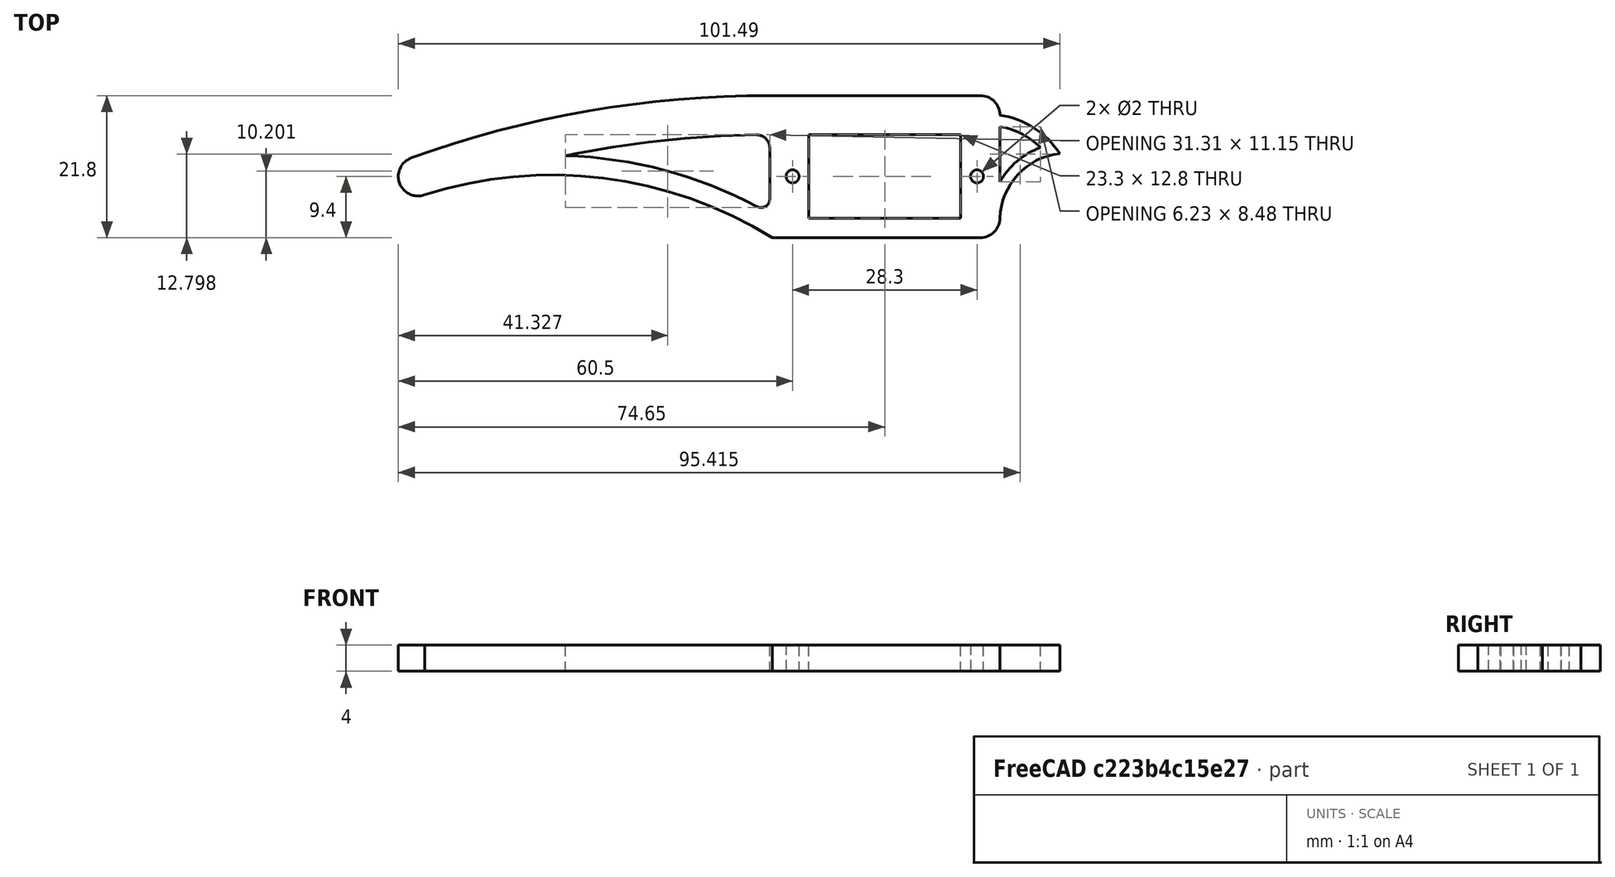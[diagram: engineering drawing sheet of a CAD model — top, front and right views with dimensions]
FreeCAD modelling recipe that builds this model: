
FCSTD DOCUMENT  (FreeCAD 0.21R33771 (Git))
Label: крак-база
License: All rights reserved
LicenseURL: https://en.wikipedia.org/wiki/All_rights_reserved
objects: Sketcher::SketchObject×1, PartDesign::Pad×1, PartDesign::Body×1
note: 4 computed .brp shape members not serialized (recipe doc carries the construction recipe); baked Part::Feature solids carry a one-line shape summary decoded from their .brp

FEATURE [Sketcher::SketchObject] Sketch
  FullyConstrained = true
  MapMode = 5
  Support = -> [XY_Plane]
  sketch-geometry (26):
    g0: LineSegment StartX=-11.65 StartY=-6.4 StartZ=0 EndX=-11.65 EndY=6.4 EndZ=0
    g1: LineSegment StartX=-11.65 StartY=6.4 StartZ=0 EndX=11.65 EndY=6.4 EndZ=0
    g2: LineSegment StartX=11.65 StartY=6.4 StartZ=0 EndX=11.65 EndY=-6.4 EndZ=0
    g3: LineSegment StartX=11.65 StartY=-6.4 StartZ=0 EndX=-11.65 EndY=-6.4 EndZ=0
    g4: GeomPoint X=0 Y=0 Z=0
    g5: LineSegment StartX=-17.65 StartY=12.4 StartZ=0 EndX=14.65 EndY=12.4 EndZ=0
    g6: LineSegment StartX=17.65 StartY=7.63618 StartZ=0 EndX=17.65 EndY=-0.84 EndZ=0
    g7: LineSegment StartX=14.65 StartY=-9.4 StartZ=0 EndX=-17.27 EndY=-9.4 EndZ=0
    g8: LineSegment StartX=-17.6662 StartY=-3.46627 StartZ=0 EndX=-17.6662 EndY=4.38856 EndZ=0
    g9: ArcOfCircle CenterX=-71.65 CenterY=0 CenterZ=0 NormalX=0 NormalY=0 NormalZ=1 AngleXU=0 Radius=3 StartAngle=1.91771 EndAngle=5.06056
    g10: ArcOfCircle CenterX=14.65 CenterY=9.4 CenterZ=0 NormalX=0 NormalY=0 NormalZ=1 AngleXU=0 Radius=3 StartAngle=6.28319 EndAngle=7.85398
    g11: GeomPoint X=17.65 Y=12.4 Z=0
    g12: ArcOfCircle CenterX=14.65 CenterY=-6.4 CenterZ=0 NormalX=0 NormalY=0 NormalZ=1 AngleXU=0 Radius=3 StartAngle=4.71239 EndAngle=6.28319
    g13: GeomPoint X=17.65 Y=-9.4 Z=0
    g14: ArcOfCircle CenterX=-18.0008 CenterY=-148.391 CenterZ=0 NormalX=0 NormalY=0 NormalZ=1 AngleXU=0 Radius=160.792 StartAngle=1.56861 EndAngle=1.91771
    g15: ArcOfCircle CenterX=-16.955 CenterY=-154.388 CenterZ=0 NormalX=0 NormalY=0 NormalZ=1 AngleXU=0 Radius=160.79 StartAngle=1.58781 EndAngle=1.77131
    g16: ArcOfCircle CenterX=-51.0881 CenterY=-64.0061 CenterZ=0 NormalX=0 NormalY=0 NormalZ=1 AngleXU=0 Radius=64.23 StartAngle=1.0163 EndAngle=1.87989
    g17: ArcOfCircle CenterX=-51.0881 CenterY=-64.0061 CenterZ=0 NormalX=0 NormalY=0 NormalZ=1 AngleXU=0 Radius=67.2192 StartAngle=1.08311 EndAngle=1.53943
    g18: Circle CenterX=-14.15 CenterY=0 CenterZ=0 NormalX=0 NormalY=0 NormalZ=1 AngleXU=0 Radius=1
    g19: Circle CenterX=14.15 CenterY=0 CenterZ=0 NormalX=0 NormalY=0 NormalZ=1 AngleXU=0 Radius=1
    g20: ArcOfCircle CenterX=-19.6562 CenterY=4.38856 CenterZ=0 NormalX=0 NormalY=0 NormalZ=1 AngleXU=0 Radius=1.99 StartAngle=2e-16 EndAngle=1.58781
    g21: ArcOfCircle CenterX=-18.9762 CenterY=-3.46627 CenterZ=0 NormalX=0 NormalY=0 NormalZ=1 AngleXU=0 Radius=1.31 StartAngle=4.2247 EndAngle=6.28319
    g22: ArcOfCircle CenterX=27.9979 CenterY=-6.77676 CenterZ=0 NormalX=0 NormalY=0 NormalZ=1 AngleXU=0 Radius=11.93 StartAngle=1.92322 EndAngle=2.62072
    g23: ArcOfCircle CenterX=15.7697 CenterY=-3.64824 CenterZ=0 NormalX=0 NormalY=0 NormalZ=1 AngleXU=0 Radius=11.44 StartAngle=0.782798 EndAngle=1.40568
    g24: ArcOfCircle CenterX=15.7697 CenterY=-3.64824 CenterZ=0 NormalX=0 NormalY=0 NormalZ=1 AngleXU=0 Radius=13.183 StartAngle=0.573993 EndAngle=1.42768
    g25: ArcOfCircle CenterX=28.0029 CenterY=-6.78453 CenterZ=0 NormalX=0 NormalY=0 NormalZ=1 AngleXU=0 Radius=10.36 StartAngle=1.68328 EndAngle=3.10447
  constraints (77):
    c: Coincident(g0,g1)
    c: Coincident(g1,g2)
    c: Coincident(g2,g3)
    c: Coincident(g3,g0)
    c: Horizontal(g1)
    c: Horizontal(g3)
    c: Vertical(g0)
    c: Vertical(g2)
    c: Symmetric(g1,g0,g4)
    c: Coincident(g4,g-1)
    c: DistanceX(g0,g1) = 23.3  'ЛЕГЛО МОТОР ДЪЛЖИНА'
    c: DistanceY(g2,g1) = 12.8  'ЛЕГЛО МОТОР ШИРИНА'
    c: Horizontal(g5)
    c: Horizontal(g7)
    c: Vertical(g6)
    c: Vertical(g8)
    c: DistanceX(g1,g11) = 6
    c: DistanceY(g1,g11) = 6
    c: DistanceX(g5,g0) = 6
    c: DistanceY(g13,g2) = 3
    c: PointOnObject(g9,g-1)
    c: Radius(g9) = 3
    c: DistanceX(g9,g0) = 60
    c: PointOnObject(g11,g5)
    c: PointOnObject(g11,g6)
    c: Tangent(g5,g10) = 1.5708
    c: PointOnObject(g13,g6)
    c: PointOnObject(g13,g7)
    c: Tangent(g7,g12) = 1.5708
    c: Radius(g10) = 3
    c: Radius(g12) = 3
    c: Coincident(g14,g5)
    c: DistanceX(g14,g0) = 61.02
    c: Radius(g15) = 160.79
    c: Coincident(g16,g7)
    c: Radius(g16) = 64.23
    c: Coincident(g17,g16)
    c: Tangent(g9,g14) = -1.5708
    c: Coincident(g15,g17)
    c: DistanceY(g9,g-1) = 2.82
    c: DistanceY(g-1,g15) = 3.18
    c: PointOnObject(g18,g-1)
    c: Radius(g18) = 1
    c: DistanceX(g18,g0) = 2.5
    c: PointOnObject(g19,g-1)
    c: Radius(g19) = 1
    c: DistanceX(g1,g19) = 2.5
    c: Tangent(g15,g20) = -1.5708
    c: Tangent(g8,g20) = -1.5708
    c: Tangent(g8,g21) = -1.5708
    c: Tangent(g17,g21) = 1.5708
    c: Radius(g20) = 1.99
    c: Radius(g21) = 1.31
    c: DistanceX(g15,g0) = 8.04
    c: DistanceX(g17,g0) = 7.94
    c: DistanceX(g1,g24) = 15.19
    c: DistanceY(g24,g1) = 2.89
    c: Radius(g23) = 11.44
    c: Radius(g22) = 11.93
    c: Coincident(g23,g22)
    c: Coincident(g6,g22)
    c: Coincident(g6,g23)
    c: DistanceX(g1,g22) = 12.23
    c: DistanceY(g22,g1) = 1.98
    c: DistanceY(g12,g-1) = 6.4
    c: DistanceX(g-1,g7) = 14.65
    c: DistanceX(g-1,g10) = 17.65
    c: DistanceX(g-1,g5) = 14.65
    c: Coincident(g24,g23)
    c: Coincident(g24,g10)
    c: Coincident(g9,g16)
    c: DistanceX(g15,g0) = 37.33
    c: DistanceX(g7,g-1) = 17.27
    c: Coincident(g25,g12)
    c: Coincident(g25,g24)
    c: Radius(g25) = 10.36
    c: DistanceY(g6,g1) = 7.24
FEATURE [PartDesign::Pad] Pad
  Direction = (0,0,1)
  Length = 4
  Length2 = 10
  Profile = -> Sketch
  ReferenceAxis = -> Sketch [N_Axis]
  Type = 0
FEATURE [PartDesign::Body] Body
  Group = -> [Sketch,Pad]
  Origin = -> Origin
  Tip = -> Pad
